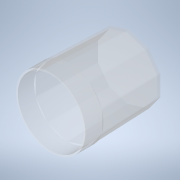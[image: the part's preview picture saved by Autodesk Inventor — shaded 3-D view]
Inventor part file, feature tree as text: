
AUTODESK INVENTOR PART (.ipt)
format: ipt  version: 2022 (Build 260153000, 153)  size: 275,456 bytes
history: native  units: mm
features: extrude x3, sketch x3, projected_geometry x2, fillet x1, shell x1
ambient origin geometry x8: Origin, YZ Plane, XZ Plane, XY Plane, X Axis, Y Axis, Z Axis, Center Point
bodies: Volumenkörper1 (feature_tree)
feature tree (10):
  extrude  "Extrusion1"  Depth=69.0mm TaperAngle=0.0deg
  fillet  "Rundung1"  Radius=3.0mm
  extrude  "Extrusion2"  Depth=65.0mm
  extrude  "Extrusion3"  Depth=2.0mm
  shell  "Wandung1"  [1 undecoded]
  sketch  "Skizze1"  dims[d0=69.0mm d1=2.0mm d2=0.0mm d3=3.0mm]
  sketch  "Skizze2"  dims[d4=2.0mm d5=65.0mm d6=0.349066mm]
  projected_geometry  "Projizierte Kontur1"
  sketch  "Skizze3"  dims[d7=20.0mm d8=0.0mm d9=2.0mm]
  projected_geometry  "Projizierte Kontur2"
note: 1 required parameter value undecoded (feature->parameter linkage not recoverable at this tier; creation-order binding heuristic only, values carry confidence <= 0.55)
